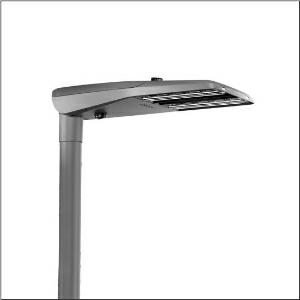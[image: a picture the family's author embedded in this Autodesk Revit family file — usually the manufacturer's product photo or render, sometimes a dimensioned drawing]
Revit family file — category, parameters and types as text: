
# Revit family: streetlight_sl_11_iq_midi___pc-l_5xc3e11y08me_a024
name_source: partatom
category: Lighting Fixtures
units: mm (PartAtom-declared; Revit-internal decimal feet)

## family parameters
Cut with Voids When Loaded = No
Host = Face
Light Source = No
Part Type = Normal
Room Calculation Point = No
Round Connector Dimension = Use Diameter
Shared = No

## types (1)
- --- (1 x LED, 9610 lm, 123.4 W, 1800K)
    Apparent Load = 123 VA
    CIE Flux Codes = 37 73 96 100 100
    Color Rendering = 70
    Color Temperature = 1800K
    Default Elevation = 1800 mm  [stored 5.90551 ft]
    Description = Streetlight SL 11 iQ midi, mast luminaire, primary light control with 3 zone facetted reflector, of plastic, silver coated, highly specular, primary optical cover: cover, of PMMA, transparent, light distribution: PC-L, light emission: direct distribution, primary light characteristic: asymmetric, left, installation type: post-top, side-entry, lamps: LED, High Power LED, rated values: 9.610lm | 123,4W | 77,9lm/W (begin service life); end service life: 9.610lm | 130,9W; at 50% lumin. flux: 4.805lm | 54,1W | 88,8lm/W, colour temperature: 1800K, colour rendering: CRI > 70, light colour: 718, light setting 1 begin service life: 100% | 9.610lm | 123,4W | 77,9lm/W | 1.800K, light setting 1 end service life: 130,9W, further light settings possible, control: pre-setting: logarithmic dimming characteristic, Street-Remote, Auto-Match, Temp-Guard, Lumen-Switch, Night-Set, Smart-Wire, Light-Fading, Desk-Remote (wireless, voltage-free reading and setting of iQ features in the workshop via application-optimized NFC function/RFID function), optimised constant luminous flux control (CLO 2.0), with cable H07RN-F 3x 1.5mm², mains connection: 230..240V, AC, 50/60Hz, connection cable pre-assembled, cable length: 12,5m, luminaire housing, of diecast aluminium, powder-coated, SITECO metallic grey (DB 702S), please order mast flange separately, inclination adjustable without tools: 0°, 5°, 10°, 15° (post-top) | 0°, -5°, -10°, -15° (side-entry), sealing non-destructively replaceable, multi-level sealing system, length: 780mm, width: 376mm, height: 118mm, mast flange for spigot size: 42mm (side-entry): 5XC10008XM4, 60/48mm (side-entry/post-top): 5XC10108XM2, 76/60mm (side-entry/post-top): 5XC10108XM1, equipment: Power, Smart Interface below and above, protection rating (complete): IP66, insulation class (complete): insulation class II (safety insulation), certification: CE, ENEC, ENEC+, VDE, UKCA, impact resistance: IK10, permissible operating ambient temperature for outdoor applications: -25..+50°C, standard-compliant lighting for roads and squares, Environmental Product Declaration (EPD) tested and certified by an independent institute, packaging unit: 1 piece

Light Distribution: PC-L
    Height = 118 mm
    Lamp = 1 x LED
    Lamp Light Flux = 9610 lm
    Lamp Power = 123.4 W
    Lamp count = 1
    Length = 780 mm
    Luminous efficacy = 78 lm/W
    Manufacturer = Siteco
    ModVariant = No
    Model = 5XC3E11Y08ME
    Number of Poles = 1
    OnlyDefault = Yes
    Power Factor = 1
    Product Name = Streetlight SL 11 iQ midi | PC-L
    Product group = mast luminaire | pylon top
    ProductGroupID = 6100
    Protection Class = Protection class II
    Protection Degree = IP 66
    RLX_Detail_Level = 1
    RLX_Emergency_Light_Flux = 0 lm
    RLX_Emergency_Type = 0
    RLX_Emergency_Type_DB = No
    RlxData = <blob elided: 74029 chars, md5=d22cf8af>
    Socket = socket
    Standby Power = 0 W
    System Light Flux = 9610 lm
    System Power = 123 W
    Type Comments = factory setting: luminous flux: 100 % | dim-lin: 254 | 553 mA
    Type Image = l_1004429.jpg
    URL = http://relux.com
    VarID = @adj_039141
    Voltage = 0 V
    Weight = 0.00 kg
    Width = 376 mm

note: [stored X ft] marks values corroborated as IEEE doubles in the binary element streams (Revit-internal decimal feet)

## geometry (parser evidence)
native form markers: Blend x4, Sweep x10
no freeform markers — native parametric forms only
